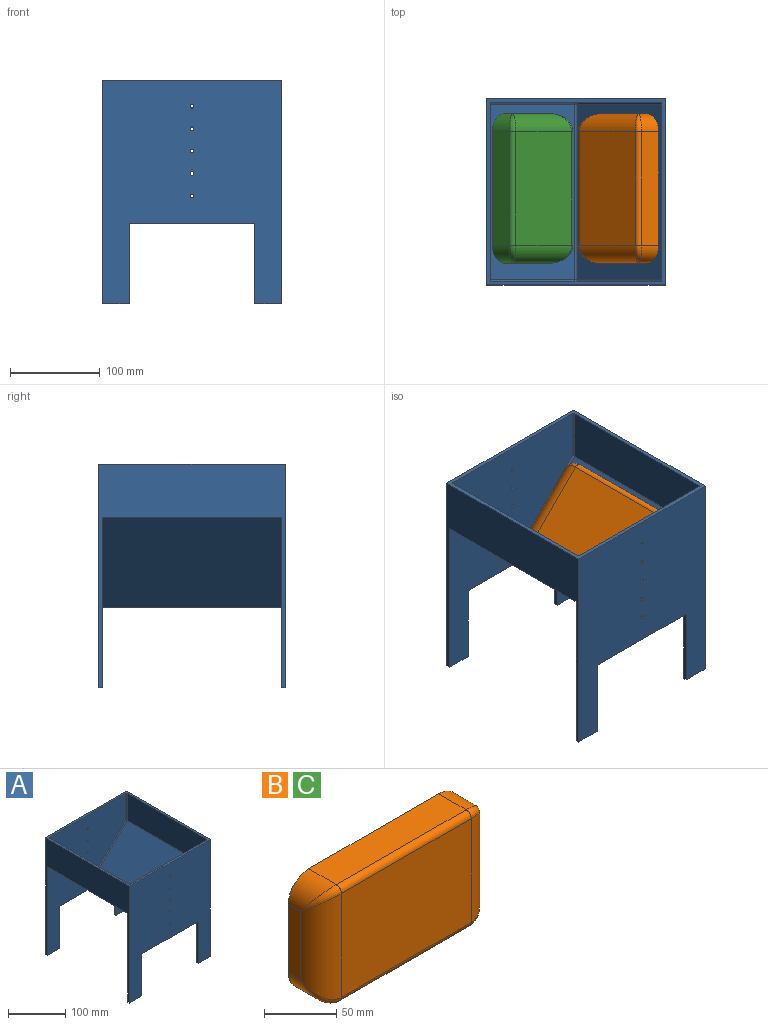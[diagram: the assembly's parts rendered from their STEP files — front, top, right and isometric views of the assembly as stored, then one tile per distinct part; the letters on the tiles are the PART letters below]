
ASSEMBLY  parts=3 mates=2
PART A: 48 faces, bbox 200x208x250 mm
  f0: plane 30x4mm, normal (0,0,-1), area 120mm2, adj f3,f11,f13,f35
  f1: plane 30x4mm, normal (0,0,-1), area 120mm2, adj f5,f13,f18,f32
  f2: plane 190x100mm, normal (0,1,0), area 7700mm2, adj f6,f10,f17,f34,f36
  f3: plane 250x200mm, normal (0,-1,0), area 37337.2mm2, adj f0,f9,f10,f13,f17,f21,f22,f23
  f4: plane 190x100mm, normal (0,-1,0), area 7700mm2, adj f6,f10,f20,f31,f33
  f5: plane 250x200mm, normal (0,1,0), area 37337.2mm2, adj f1,f9,f10,f13,f20,f26,f27,f28
  f6: plane 200x100mm, normal (-0.71,0,-0.71), area 28284.3mm2, adj f2,f4,f10,f12
  f7: plane 196x94.59mm, normal (0.71,0,0.71), area 26217.8mm2, adj f8,f40,f43,f44
  f8: plane 196x58.34mm, normal (1,0,0), area 11435.3mm2, adj f7,f9,f38,f42
  f9: plane 208x200mm, normal (0,0,1), area 3203.4mm2, adj f3,f5,f8,f10,f13,f14,f16,f19
  f10: plane 250x208mm, normal (-1,0,0), area 14000mm2, adj f2,f3,f4,f5,f6,f9,f17,f20
  f11: plane 190x100mm, normal (0,1,0), area 7700mm2, adj f0,f12,f13,f35,f36
  f12: plane 200x100mm, normal (0.71,0,-0.71), area 28284.3mm2, adj f6,f11,f13,f18
  f13: plane 250x208mm, normal (1,0,0), area 14000mm2, adj f0,f1,f3,f5,f9,f11,f12,f18
  f14: plane 196x58.34mm, normal (-1,0,0), area 11435.3mm2, adj f9,f15,f37,f47
  f15: plane 196x94.59mm, normal (-0.71,0,0.71), area 26217.8mm2, adj f14,f39,f43,f46
  f16: plane 188x151.51mm, normal (0,1,0), area 19585.9mm2, adj f9,f21,f22,f23,f24,f25,f37,f38
  f17: plane 30x4mm, normal (0,0,-1), area 120mm2, adj f2,f3,f10,f34
  f18: plane 190x100mm, normal (0,-1,0), area 7700mm2, adj f1,f12,f13,f31,f32
  f19: plane 188x151.51mm, normal (0,-1,0), area 19585.9mm2, adj f9,f26,f27,f28,f29,f30,f42,f44
  f20: plane 30x4mm, normal (0,0,-1), area 120mm2, adj f4,f5,f10,f33
  f21: cylinder r=2mm len=4mm, axis (0,-1,0), area 50.3mm2, adj f3,f16
  f22: cylinder r=2mm len=4mm, axis (0,-1,0), area 50.3mm2, adj f3,f16
  f23: cylinder r=2mm len=4mm, axis (0,-1,0), area 50.3mm2, adj f3,f16
  f24: cylinder r=2mm len=4mm, axis (0,-1,0), area 50.3mm2, adj f3,f16
  f25: cylinder r=2mm len=4mm, axis (0,-1,0), area 50.3mm2, adj f3,f16
  f26: cylinder r=2mm len=4mm, axis (0,1,0), area 50.3mm2, adj f5,f19
  f27: cylinder r=2mm len=4mm, axis (0,1,0), area 50.3mm2, adj f5,f19
  f28: cylinder r=2mm len=4mm, axis (0,1,0), area 50.3mm2, adj f5,f19
  f29: cylinder r=2mm len=4mm, axis (0,1,0), area 50.3mm2, adj f5,f19
  f30: cylinder r=2mm len=4mm, axis (0,1,0), area 50.3mm2, adj f5,f19
  f31: plane 140x4mm, normal (0,0,-1), area 560mm2, adj f4,f5,f18,f32,f33
  f32: plane 90x4mm, normal (-1,0,0), area 360mm2, adj f1,f5,f18,f31
  f33: plane 90x4mm, normal (1,0,0), area 360mm2, adj f4,f5,f20,f31
  f34: plane 90x4mm, normal (1,0,0), area 360mm2, adj f2,f3,f17,f36
  f35: plane 90x4mm, normal (-1,0,0), area 360mm2, adj f0,f3,f11,f36
  f36: plane 140x4mm, normal (0,0,-1), area 560mm2, adj f2,f3,f11,f34,f35
  f37: cylinder r=2mm len=58.34mm, axis (0,0,1), area 182.3mm2, adj f9,f14,f16,f39
  f38: cylinder r=2mm len=58.34mm, axis (0,0,-1), area 182.3mm2, adj f8,f9,f16,f40
  f39: cylinder r=2mm len=96mm, axis (0.71,0,0.71), area 419.3mm2, adj f15,f16,f37,f41
  f40: cylinder r=2mm len=96mm, axis (0.71,0,-0.71), area 419.3mm2, adj f7,f16,f38,f41
  f41: sphere r=2mm, area 6.3mm2, adj f39,f40,f43
  f42: cylinder r=2mm len=58.34mm, axis (0,0,-1), area 182.3mm2, adj f8,f9,f19,f44
  f43: cylinder r=2mm len=196mm, axis (0,1,0), area 615.8mm2, adj f7,f15,f41,f45
  f44: cylinder r=2mm len=96mm, axis (0.71,0,-0.71), area 419.3mm2, adj f7,f19,f42,f45
  f45: sphere r=2mm, area 6.3mm2, adj f43,f44,f46
  f46: cylinder r=2mm len=96mm, axis (0.71,0,0.71), area 419.3mm2, adj f15,f19,f45,f47
  f47: cylinder r=2mm len=58.34mm, axis (0,0,1), area 182.3mm2, adj f9,f14,f19,f46
PART B: 18 faces, bbox 167x32x98 mm
  f0: plane 58x12mm, normal (-1,0,0), area 696mm2, adj f5,f13,f15,f17
  f1: plane 127x27mm, normal (0,0,-1), area 3429mm2, adj f5,f6,f12,f17
  f2: plane 58x12mm, normal (1,0,0), area 696mm2, adj f5,f8,f10,f12
  f3: plane 127x27mm, normal (0,0,1), area 3429mm2, adj f5,f7,f8,f13
  f4: plane 127x88mm, normal (0,-1,0), area 11176mm2, adj f6,f7,f10,f15
  f5: plane 167x98mm, normal (0,1,0), area 16022.6mm2, adj f0,f1,f2,f3,f8,f12,f13,f17
  f6: cylinder r=5mm len=127mm, axis (-1,0,0), area 997.5mm2, adj f1,f4,f11,f16
  f7: cylinder r=5mm len=127mm, axis (1,0,0), area 997.5mm2, adj f3,f4,f9,f14
  f8: cylinder r=20mm len=27mm, axis (0,-1,0), area 677mm2, adj f2,f3,f5,f9
  f9: bspline ~20.82x20mm, area 169mm2, adj f7,f8,f10
  f10: cylinder r=20mm len=88mm, axis (0,0,-1), area 2422.1mm2, adj f2,f4,f9,f11
  f11: bspline ~20.82x20mm, area 169mm2, adj f6,f10,f12
  f12: cylinder r=20mm len=27mm, axis (0,1,0), area 677mm2, adj f1,f2,f5,f11
  f13: cylinder r=20mm len=27mm, axis (0,1,0), area 677mm2, adj f0,f3,f5,f14
  f14: bspline ~20.82x20mm, area 169mm2, adj f7,f13,f15
  f15: cylinder r=20mm len=88mm, axis (0,0,1), area 2422.1mm2, adj f0,f4,f14,f16
  f16: bspline ~20.82x20mm, area 169mm2, adj f6,f15,f17
  f17: cylinder r=20mm len=27mm, axis (0,-1,0), area 677mm2, adj f0,f1,f5,f16
PART C: same geometry as B
PLACE A t=(-59.63,-11.32,-0.34)mm fixed
PLACE B rot(axis=(-0.68,-0.68,0.28),148.6deg) t=(32.72,-91.14,97.67)mm
PLACE C rot(axis=(-0.36,-0.36,0.86),98.4deg) t=(-83.8,-90.87,29.49)mm
MATE planar C.f5 <-> A.f7  axis (-0.71,0,-0.71) through (-118.45,-7.37,64.13)mm
MATE planar B.f5 <-> A.f15  axis (0.71,0,-0.71) through (-36.57,-7.64,28.37)mm
